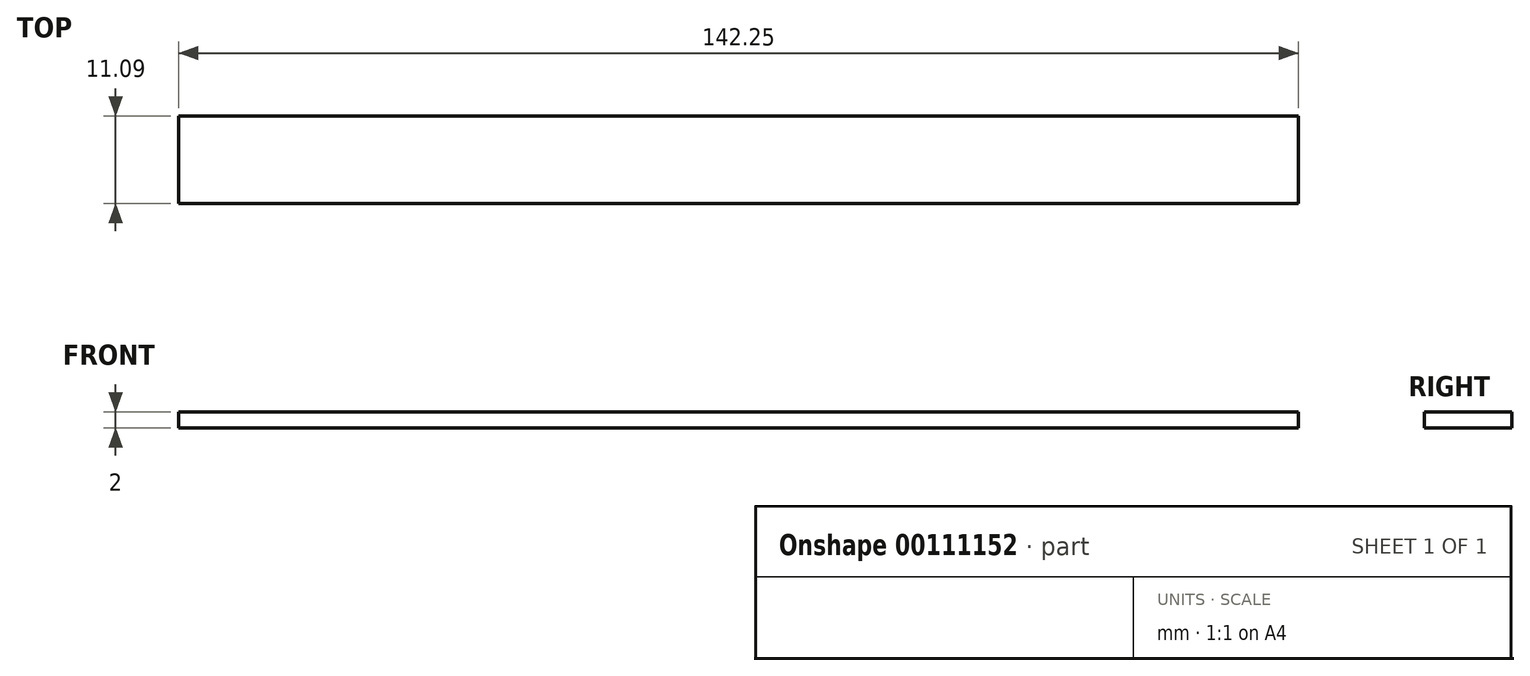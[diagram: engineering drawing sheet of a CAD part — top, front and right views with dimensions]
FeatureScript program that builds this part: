
annotation { "Feature Type Name" : "Feature", "Feature Type Description" : "" }
export const myFeature = defineFeature(function(context is Context, id is Id, definition is map)
    precondition{}
    {
        {
            var Q0;
            Q0=qCreatedBy(makeId("Top.planeOp"),FACE);
            var sketch = newSketch(context, id + "F0", { "sketchPlane" : qUnion([Q0])});
            skLineSegment(sketch, "E0.bottom", {"start": v(-75.64, 21.33) * mm, "end": v(66.6, 21.33) * mm});
            skLineSegment(sketch, "E0.top", {"start": v(-75.64, 10.24) * mm, "end": v(66.6, 10.24) * mm});
            skLineSegment(sketch, "E0.left", {"start": v(-75.64, 21.33) * mm, "end": v(-75.64, 10.24) * mm});
            skLineSegment(sketch, "E0.right", {"start": v(66.6, 21.33) * mm, "end": v(66.6, 10.24) * mm});
            skSolve(sketch);
        }
        {
            var Q0;
            Q0=makeQuery(id+"F0.imprint","IMPRINT",FACE,{"disambiguationData":[TD([[makeQuery(id+"F0.imprint","IMPRINT",EDGE,{"derivedFrom":sQuery(id+"F0.wireOp",EDGE,"E0.bottom")}),-1.0]])]});
            extrude(context, id + "F1", {"entities" : qUnion([Q0]), "depth" : 2 * mm});
        }
    });
